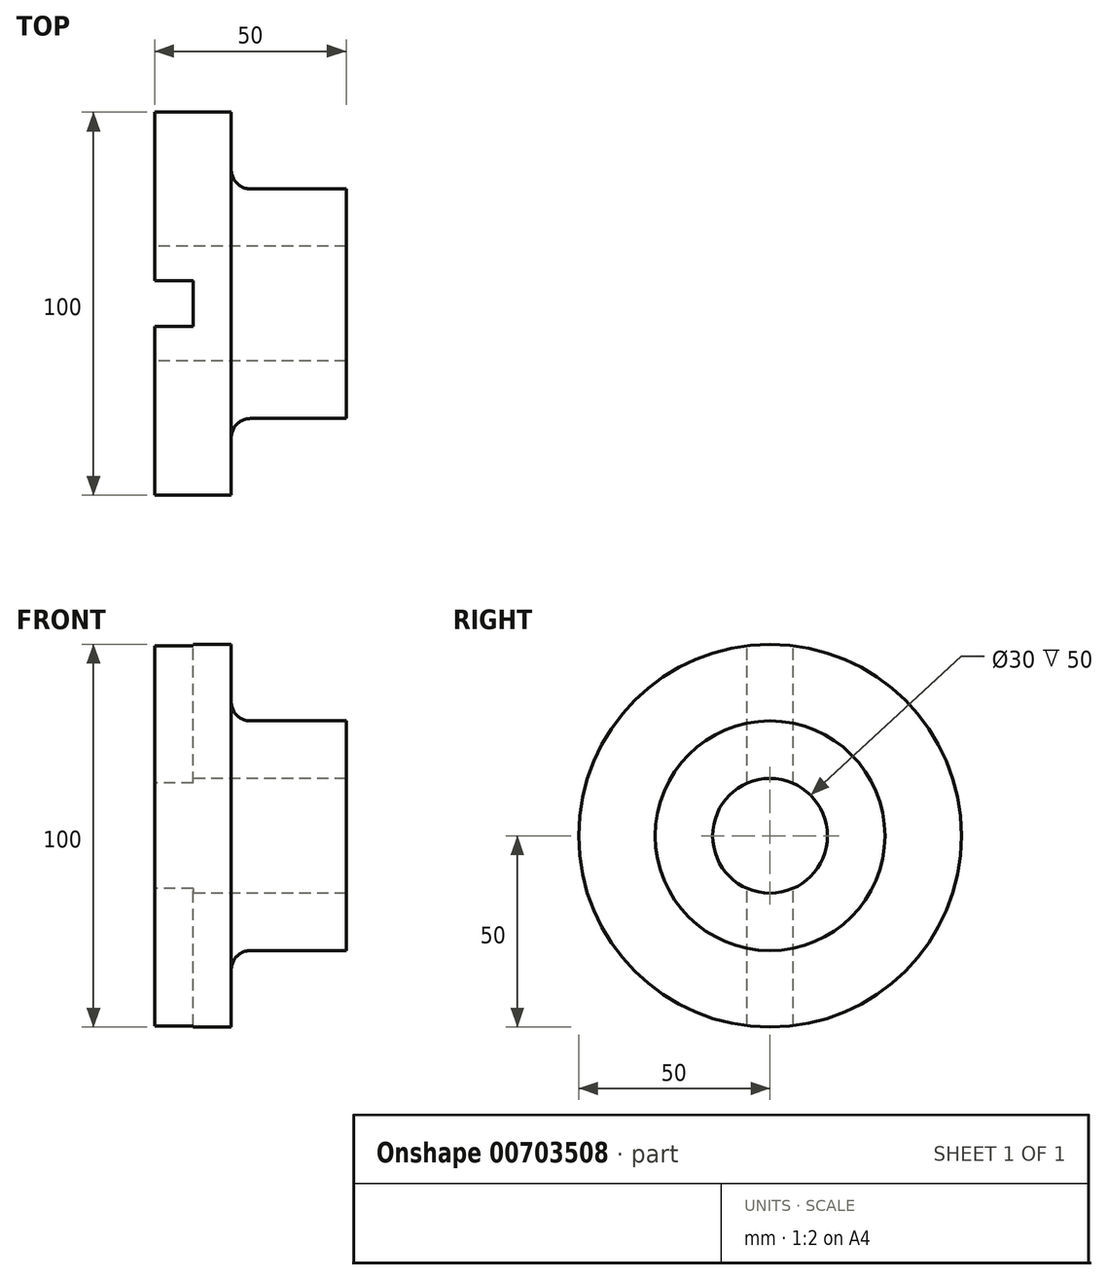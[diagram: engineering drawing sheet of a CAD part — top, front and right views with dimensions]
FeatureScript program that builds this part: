
annotation { "Feature Type Name" : "Feature", "Feature Type Description" : "" }
export const myFeature = defineFeature(function(context is Context, id is Id, definition is map)
    precondition{}
    {
        {
            var Q0;
            Q0=qCreatedBy(makeId("Top.planeOp"),FACE);
            var sketch = newSketch(context, id + "F0", { "sketchPlane" : qUnion([Q0])});
            skLineSegment(sketch, "E0", {"start": v(-53.77, 0) * mm, "end": v(-53.77, -35) * mm});
            skLineSegment(sketch, "E1", {"start": v(-53.77, -35) * mm, "end": v(-3.77, -35) * mm});
            skLineSegment(sketch, "E2", {"start": v(-3.77, -35) * mm, "end": v(-3.77, -20) * mm});
            skLineSegment(sketch, "E3", {"start": v(-3.77, -20) * mm, "end": v(-28.77, -20) * mm});
            skLineSegment(sketch, "E4", {"start": v(-33.77, -15) * mm, "end": v(-33.77, 0) * mm});
            skLineSegment(sketch, "E5", {"start": v(-33.77, 0) * mm, "end": v(-53.77, 0) * mm});
            skPoint(sketch, "E6.visualSharp", {"position": v(-33.77, -20) * mm});
            skArc(sketch, "E6.filletArc", {"start": v(-33.77, -15) * mm, "mid": v(-32.3, -18.54) * mm, "end": v(-28.77, -20) * mm});
            skLineSegment(sketch, "E7", {"start": v(-53.77, -35) * mm, "end": v(-53.77, -50) * mm});
            skLineSegment(sketch, "E8", {"start": v(-53.77, -50) * mm, "end": v(-43.77, -50) * mm});
            skLineSegment(sketch, "E9", {"start": v(-43.77, -50) * mm, "end": v(-43.77, -44) * mm});
            skLineSegment(sketch, "E10", {"start": v(-43.77, -44) * mm, "end": v(-53.77, -44) * mm});
            skLineSegment(sketch, "E11.MirrorCS", {"start": v(-43.77, -50) * mm, "end": v(-43.77, -56) * mm});
            skLineSegment(sketch, "E12.MirrorCS", {"start": v(-43.77, -56) * mm, "end": v(-53.77, -56) * mm});
            skLineSegment(sketch, "E13.MirrorCS", {"start": v(-53.77, -65) * mm, "end": v(-53.77, -50) * mm});
            skLineSegment(sketch, "E14", {"start": v(-53.77, -50) * mm, "end": v(46.23, -50) * mm});
            skSolve(sketch);
        }
        {
            var Q0;
            Q0=makeQuery(id+"F0.imprint","IMPRINT",FACE,{"disambiguationData":[TD([[makeQuery(id+"F0.imprint","IMPRINT",EDGE,{"derivedFrom":sQuery(id+"F0.wireOp",EDGE,"E0")}),1.0]])]});
            var Q1;
            Q1=sQuery(id+"F0.wireOp",EDGE,"E14");
            revolve(context, id + "F1", {"surfaceOperationType" : NewSurfaceOperationType.NEW, "entities" : qUnion([Q0]), "axis" : qUnion([Q1]), "revolveType" : RevolveType.FULL});
        }
        {
            var Q0;
            {var subQ0=sQuery(id+"F0.wireOp",EDGE,"E11.MirrorCS");Q0=makeQuery(id+"F0.imprint","IMPRINT",FACE,{"disambiguationData":[TD([[makeQuery(id+"F0.imprint","IMPRINT",EDGE,{"derivedFrom":subQ0}),-1.0]])]});}
            var Q1;
            {var subQ4=sQuery(id+"F0.wireOp",EDGE,"E9");Q1=makeQuery(id+"F0.imprint","IMPRINT",FACE,{"disambiguationData":[TD([[makeQuery(id+"F0.imprint","IMPRINT",EDGE,{"derivedFrom":subQ4}),1.0]])]});}
            extrude(context, id + "F2", {"entities" : qUnion([Q0, Q1]), "operationType" : NewBodyOperationType.REMOVE, "endBound" : BoundingType.THROUGH_ALL, "oppositeDirection" : true, "depth" : 25 * mm, "offsetDistance" : 25 * mm, "hasSecondDirection" : true, "secondDirectionBound" : SecondDirectionBoundingType.THROUGH_ALL, "secondDirectionOppositeDirection" : false, "secondDirectionDepth" : 25 * mm});
        }
    });
